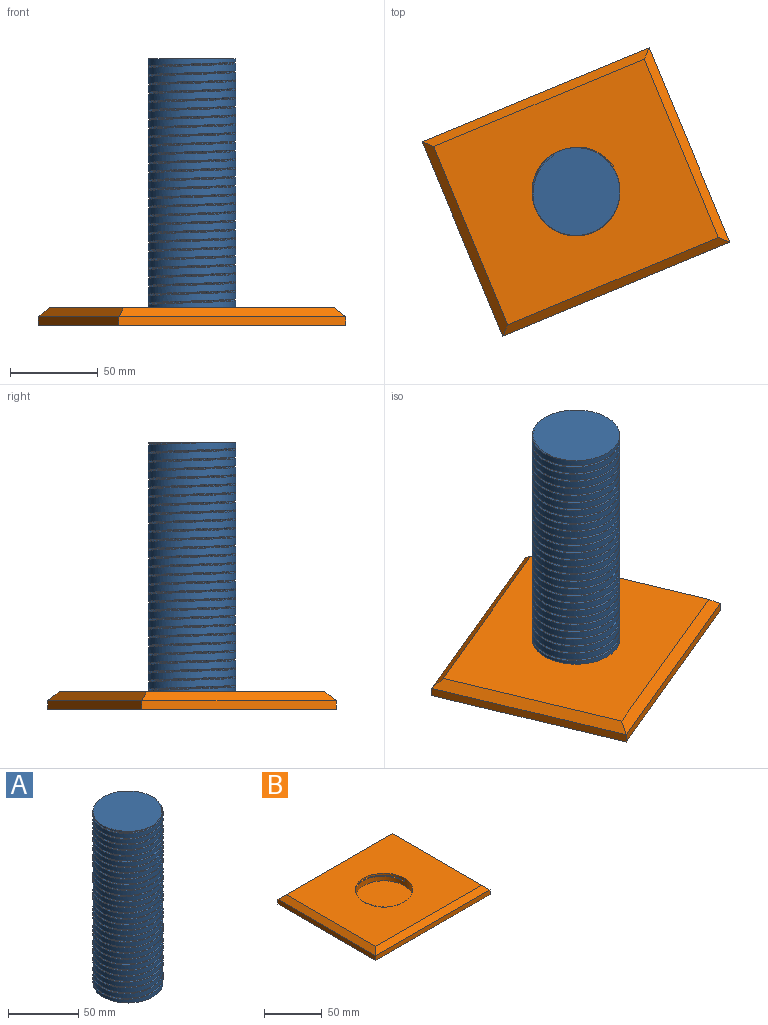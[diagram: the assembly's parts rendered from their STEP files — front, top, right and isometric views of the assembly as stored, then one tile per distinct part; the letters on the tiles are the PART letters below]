
ASSEMBLY  parts=2 mates=1
PART A: 6 faces, bbox 50.2x57.9x151.2 mm
  f0: cylinder r=25mm len=150mm, axis (0,0,-1), area 17856.8mm2, adj f1,f2,f3,f4,f5
  f1: plane 50.16x50.16mm, normal (0,0,1), area 1950.2mm2, adj f0,f4,f5
  f2: plane 50x50mm, normal (0,0,-1), area 1963.5mm2, adj f0
  f3: plane 1x0.87mm, normal (0,1,0), area 0.4mm2, adj f0,f4,f5
  f4: bspline ~150.5x57.74mm, area 4606.6mm2, adj f0,f1,f3,f5
  f5: bspline ~150.5x57.74mm, area 4613.6mm2, adj f0,f1,f3,f4
PART B: 16 faces, bbox 140.2x120.2x11.1 mm
  f0: plane 140x5mm, normal (0,1,0), area 700mm2, adj f1,f3,f4,f7
  f1: plane 120x5mm, normal (-1,0,0), area 600mm2, adj f0,f2,f4,f6
  f2: plane 140x5mm, normal (0,-1,0), area 700mm2, adj f1,f3,f4,f8
  f3: plane 120x5mm, normal (1,0,0), area 600mm2, adj f0,f2,f4,f9
  f4: plane 140x120mm, normal (0,0,-1), area 16800mm2, adj f0,f1,f2,f3
  f5: plane 130.22x110.22mm, normal (0,0,1), area 12322.6mm2, adj f6,f7,f8,f9,f10,f11,f14,f15
  f6: plane 120x5mm, normal (-0.71,0,0.71), area 813.2mm2, adj f1,f5,f7,f8
  f7: plane 140x5mm, normal (0,0.71,0.71), area 954.6mm2, adj f0,f5,f6,f9
  f8: plane 140x5mm, normal (0,-0.71,0.71), area 954.6mm2, adj f2,f5,f6,f9
  f9: plane 120x5mm, normal (0.71,0,0.71), area 813.2mm2, adj f3,f5,f7,f8
  f10: cylinder r=25mm len=50mm, axis (0,0,1), area 1035.7mm2, adj f5,f11,f12,f13,f15
  f11: cylinder r=25mm len=50mm, axis (0,0,1), area 119.1mm2, adj f5,f10,f14
  f12: plane 50x50mm, normal (0,0,1), area 1963.5mm2, adj f10
  f13: plane 1x0.87mm, normal (0,1,0), area 0.4mm2, adj f10,f14,f15
  f14: bspline ~52.27x51.73mm, area 96mm2, adj f5,f11,f13,f15
  f15: bspline ~59.74x51.73mm, area 111.7mm2, adj f5,f10,f13,f14
PLACE A rot(axis=(0,0,-1),157.5deg) t=(-104.41,-35.79,-97.06)mm
PLACE B rot(axis=(0,0,-1),157.5deg) t=(-104.41,-35.79,-89.06)mm
MATE planar B.f10 <-> A.f0  axis (0,0,1) through (-104.41,-35.79,-97.06)mm
